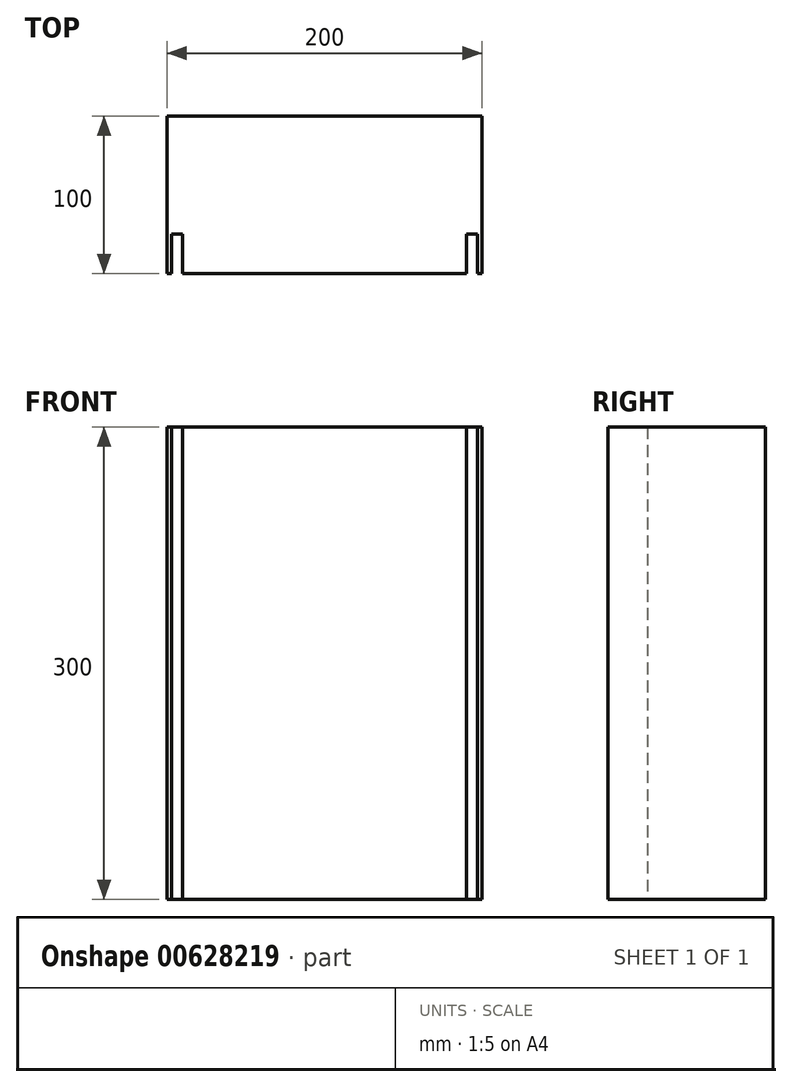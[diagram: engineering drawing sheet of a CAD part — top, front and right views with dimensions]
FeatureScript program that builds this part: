
annotation { "Feature Type Name" : "Feature", "Feature Type Description" : "" }
export const myFeature = defineFeature(function(context is Context, id is Id, definition is map)
    precondition{}
    {
        {
            var Q0;
            Q0=qCreatedBy(makeId("Front.planeOp"),FACE);
            var sketch = newSketch(context, id + "F0", { "sketchPlane" : qUnion([Q0])});
            skLineSegment(sketch, "E0.bottom", {"start": v(100, -150) * mm, "end": v(-100, -150) * mm});
            skLineSegment(sketch, "E0.top", {"start": v(100, 150) * mm, "end": v(-100, 150) * mm});
            skLineSegment(sketch, "E0.left", {"start": v(100, -150) * mm, "end": v(100, 150) * mm});
            skLineSegment(sketch, "E0.right", {"start": v(-100, -150) * mm, "end": v(-100, 150) * mm});
            skPoint(sketch, "E0.middle", {"position": v(0, 0) * mm});
            skSolve(sketch);
        }
        {
            var Q0;
            Q0=makeQuery(id+"F0.imprint","IMPRINT",FACE,{"disambiguationData":[TD([[makeQuery(id+"F0.imprint","IMPRINT",EDGE,{"derivedFrom":sQuery(id+"F0.wireOp",EDGE,"E0.bottom")}),-1.0]])]});
            extrude(context, id + "F1", {"entities" : qUnion([Q0]), "depth" : 100 * mm, "offsetDistance" : 25 * mm});
        }
        {
            var Q0;
            Q0=makeQuery(id+"F1.opExtrude","CAP_FACE",FACE,{"disambiguationData":[OSD([sQuery(id+"F0.wireOp",EDGE,"E0.bottom"),sQuery(id+"F0.wireOp",EDGE,"E0.top"),sQuery(id+"F0.wireOp",EDGE,"E0.left"),sQuery(id+"F0.wireOp",EDGE,"E0.right")])],"isStart":false});
            var sketch = newSketch(context, id + "F2", { "sketchPlane" : qUnion([Q0])});
            skLineSegment(sketch, "E1", {"start": v(-97.17, 150) * mm, "end": v(-97.17, -150) * mm});
            skLineSegment(sketch, "E2", {"start": v(-97.17, -150) * mm, "end": v(-90.17, -150) * mm});
            skLineSegment(sketch, "E3", {"start": v(-90.17, -150) * mm, "end": v(-90.17, 150) * mm});
            skLineSegment(sketch, "E4", {"start": v(-90.17, 150) * mm, "end": v(-97.17, 150) * mm});
            skLineSegment(sketch, "E5", {"start": v(97.17, 150) * mm, "end": v(97.17, -150) * mm});
            skLineSegment(sketch, "E6", {"start": v(97.17, -150) * mm, "end": v(90.17, -150) * mm});
            skLineSegment(sketch, "E7", {"start": v(90.17, -150) * mm, "end": v(90.17, 150) * mm});
            skLineSegment(sketch, "E8", {"start": v(90.17, 150) * mm, "end": v(97.17, 150) * mm});
            skLineSegment(sketch, "E9", {"start": v(97.17, 150) * mm, "end": v(100, 150) * mm});
            skLineSegment(sketch, "E10", {"start": v(-100, 150) * mm, "end": v(-97.17, 150) * mm});
            skLineSegment(sketch, "E11", {"start": v(-100, -150) * mm, "end": v(-97.17, -150) * mm});
            skSolve(sketch);
        }
        {
            var Q0;
            Q0=makeQuery(id+"F2.imprint","IMPRINT",FACE,{"disambiguationData":[TD([[makeQuery(id+"F2.imprint","IMPRINT",EDGE,{"derivedFrom":sQuery(id+"F2.wireOp",EDGE,"E1")}),1.0]])]});
            var Q1;
            Q1=makeQuery(id+"F2.imprint","IMPRINT",FACE,{"disambiguationData":[TD([[makeQuery(id+"F2.imprint","IMPRINT",EDGE,{"derivedFrom":sQuery(id+"F2.wireOp",EDGE,"E5")}),-1.0]])]});
            extrude(context, id + "F3", {"entities" : qUnion([Q0, Q1]), "operationType" : NewBodyOperationType.REMOVE, "oppositeDirection" : true, "depth" : 25 * mm, "offsetDistance" : 25 * mm});
        }
    });
